# Revit family: Haworth_Mex-Hi_Ottoman_PRELIMINARY
name_source: partatom
category: Furniture
revit_build: Autodesk Revit 2018 (Build: 20170223_1515(x64)
units: mm (PartAtom-declared; Revit-internal decimal feet)

## family parameters
Always vertical = Yes
Cut with Voids When Loaded = No
OmniClass Number = 23.40.70.14.64.21
OmniClass Title = Systems Furniture
Room Calculation Point = No
Shared = No
Work Plane-Based = No

## types (2) — shared parameters
Actual Depth = 43.3 "
Actual Height = 10.2 "
Actual Width = 51.2 "
Assembly Code = E2020200
Description = Haworth - Cassina - Mex-Hi - Ottoman
Manufacturer = Haworth
Model = HCCSMHTO
Revision Number = 1
Size = Verify Final Dim. w/ Haworth
Sustainability Info = https://www.haworth.com
Top Offset = 12.69 "
Tray Depth = 43.3 "
Tray Width = 15.3 "
URL = https://www.haworth.com
URL - Product = https://www.haworth.com
Warranty = http://www.haworth.com

## per-type parameters (varying)
| type | Stone Top | Wood Tray |
| Ottoman with Stone Top | Yes | No |
| Ottoman with Wood Tray | No | Yes |

## geometry (parser evidence)
native form markers: Sweep x11
no freeform markers — native parametric forms only
